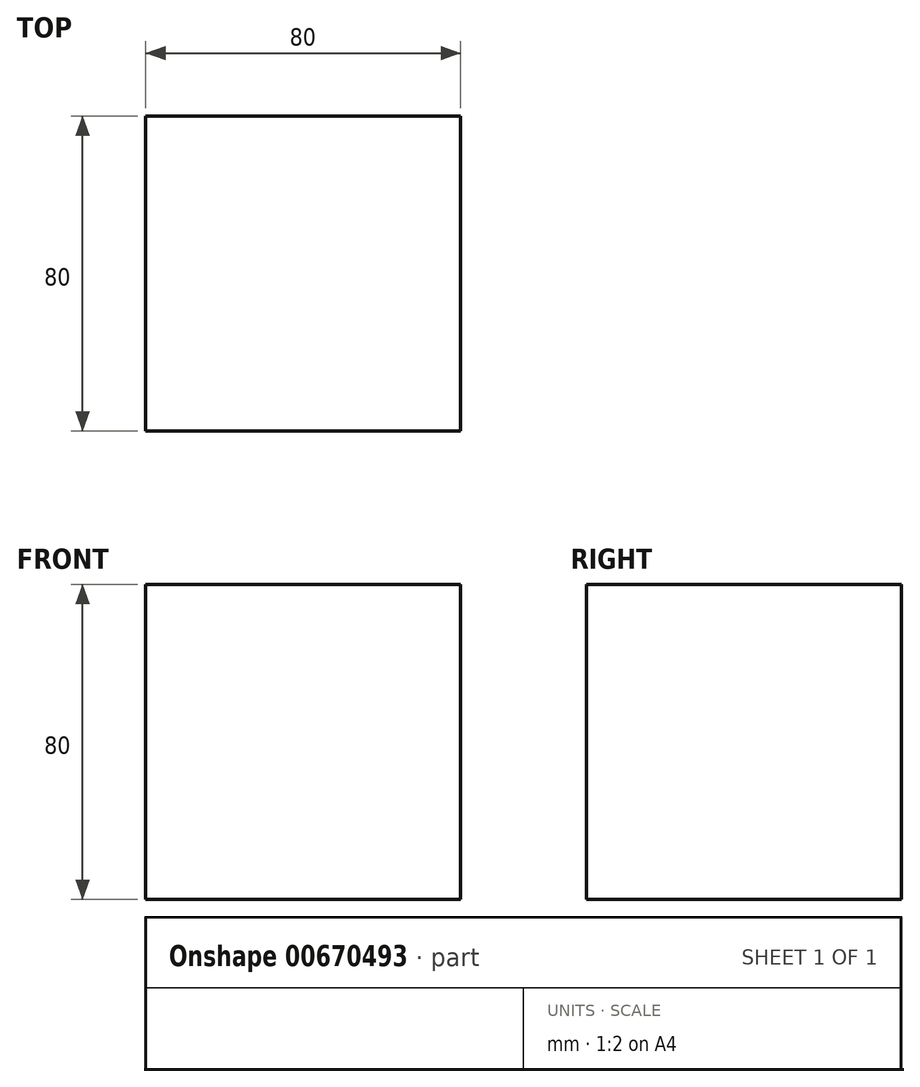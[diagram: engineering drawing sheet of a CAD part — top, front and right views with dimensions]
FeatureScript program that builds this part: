
annotation { "Feature Type Name" : "Feature", "Feature Type Description" : "" }
export const myFeature = defineFeature(function(context is Context, id is Id, definition is map)
    precondition{}
    {
        {
            var Q0;
            Q0=qCreatedBy(makeId("Top.planeOp"),FACE);
            var sketch = newSketch(context, id + "F0", { "sketchPlane" : qUnion([Q0])});
            skLineSegment(sketch, "E0.bottom", {"start": v(47.34, 0) * mm, "end": v(-32.66, 0) * mm});
            skLineSegment(sketch, "E0.top", {"start": v(47.34, -80) * mm, "end": v(-32.66, -80) * mm});
            skLineSegment(sketch, "E0.left", {"start": v(47.34, 0) * mm, "end": v(47.34, -80) * mm});
            skLineSegment(sketch, "E0.right", {"start": v(-32.66, 0) * mm, "end": v(-32.66, -80) * mm});
            skLineSegment(sketch, "E1", {"start": v(47.34, 0) * mm, "end": v(47.34, 0) * mm});
            skCircle(sketch, "E2", {"center": v(-25.02, -1.7) * mm, "radius": 1.5 * mm});
            skCircle(sketch, "E3", {"center": v(18.56, -15.12) * mm, "radius": 1.5 * mm});
            skLineSegment(sketch, "E4.bottom", {"start": v(0, -22.2) * mm, "end": v(-20, -22.2) * mm});
            skLineSegment(sketch, "E4.top", {"start": v(0, -32.2) * mm, "end": v(-20, -32.2) * mm});
            skLineSegment(sketch, "E4.left", {"start": v(0, -22.2) * mm, "end": v(0, -32.2) * mm});
            skLineSegment(sketch, "E4.right", {"start": v(-20, -22.2) * mm, "end": v(-20, -32.2) * mm});
            skLineSegment(sketch, "E5", {"start": v(-10.82, -32.2) * mm, "end": v(-10.82, -52.2) * mm});
            skLineSegment(sketch, "E6", {"start": v(-10.82, -52.2) * mm, "end": v(19.18, -52.2) * mm});
            skLineSegment(sketch, "E7", {"start": v(-10.82, -47.81) * mm, "end": v(19.18, -47.81) * mm});
            skLineSegment(sketch, "E8.bottom", {"start": v(24.63, -35.42) * mm, "end": v(14.63, -35.42) * mm});
            skLineSegment(sketch, "E8.top", {"start": v(24.63, -45.42) * mm, "end": v(14.63, -45.42) * mm});
            skLineSegment(sketch, "E8.left", {"start": v(24.63, -35.42) * mm, "end": v(24.63, -45.42) * mm});
            skLineSegment(sketch, "E8.right", {"start": v(14.63, -35.42) * mm, "end": v(14.63, -45.42) * mm});
            skLineSegment(sketch, "E9", {"start": v(19.18, -47.81) * mm, "end": v(19.18, -45.42) * mm});
            skLineSegment(sketch, "E10", {"start": v(19.18, -52.2) * mm, "end": v(23.46, -52.2) * mm});
            skLineSegment(sketch, "E11", {"start": v(23.46, -52.2) * mm, "end": v(23.46, -45.42) * mm});
            skLineSegment(sketch, "E12.bottom", {"start": v(43.32, -66.85) * mm, "end": v(-26.68, -66.85) * mm});
            skLineSegment(sketch, "E12.top", {"start": v(43.32, -76.7) * mm, "end": v(-28.41, -76.7) * mm});
            skLineSegment(sketch, "E12.left", {"start": v(43.32, -66.85) * mm, "end": v(43.32, -76.7) * mm});
            skLineSegment(sketch, "E12.right", {"start": v(-26.68, -66.85) * mm, "end": v(-28.41, -76.7) * mm});
            skLineSegment(sketch, "E13.bottom", {"start": v(-1.5, -24.06) * mm, "end": v(-18.5, -24.06) * mm});
            skLineSegment(sketch, "E13.top", {"start": v(-1.5, -30.38) * mm, "end": v(-18.5, -30.38) * mm});
            skLineSegment(sketch, "E13.left", {"start": v(-1.5, -24.06) * mm, "end": v(-1.5, -30.38) * mm});
            skLineSegment(sketch, "E13.right", {"start": v(-18.5, -24.06) * mm, "end": v(-18.5, -30.38) * mm});
            skPoint(sketch, "E14", {"position": v(-15.12, -7.6) * mm});
            skPoint(sketch, "E15", {"position": v(-13.48, -3.35) * mm});
            skPoint(sketch, "E16", {"position": v(-5.42, -3.35) * mm});
            skPoint(sketch, "E17", {"position": v(-5.2, -3.35) * mm});
            skPoint(sketch, "E18", {"position": v(-8.25, -3.35) * mm});
            skPoint(sketch, "E19", {"position": v(-9.34, -3.35) * mm});
            skPoint(sketch, "E20", {"position": v(-10.54, -3.35) * mm});
            skPoint(sketch, "E21", {"position": v(-11.52, -3.35) * mm});
            skLineSegment(sketch, "E22", {"start": v(-15.12, -7.6) * mm, "end": v(-15.12, -22.2) * mm});
            skLineSegment(sketch, "E23", {"start": v(-13.48, -3.35) * mm, "end": v(-13.48, -22.2) * mm});
            skLineSegment(sketch, "E24", {"start": v(-10.54, -3.35) * mm, "end": v(-10.54, -22.2) * mm});
            skLineSegment(sketch, "E25", {"start": v(-11.52, -3.35) * mm, "end": v(-11.52, -22.2) * mm});
            skLineSegment(sketch, "E26", {"start": v(-9.34, -3.35) * mm, "end": v(-9.34, -22.2) * mm});
            skLineSegment(sketch, "E27", {"start": v(-8.25, -3.35) * mm, "end": v(-8.25, -22.2) * mm});
            skLineSegment(sketch, "E28", {"start": v(-5.2, -3.35) * mm, "end": v(-5.2, -22.2) * mm});
            skLineSegment(sketch, "E29", {"start": v(-5.42, -3.35) * mm, "end": v(-5.42, -22.2) * mm});
            skLineSegment(sketch, "E30", {"start": v(-20, -27.2) * mm, "end": v(-30.25, -27.2) * mm});
            skLineSegment(sketch, "E31", {"start": v(-30.25, -27.2) * mm, "end": v(-30.25, -76.92) * mm});
            skLineSegment(sketch, "E32", {"start": v(-30.25, -76.92) * mm, "end": v(-26.71, -76.7) * mm});
            skLineSegment(sketch, "E33", {"start": v(-30.25, -73.39) * mm, "end": v(-27.55, -73.86) * mm});
            skPoint(sketch, "E33.endSnap0", {"position": v(-27.55, -71.77) * mm});
            skLineSegment(sketch, "E34.bottom", {"start": v(-22.08, -14.98) * mm, "end": v(-22.08, -14.98) * mm});
            skLineSegment(sketch, "E34.top", {"start": v(-22.08, -14.98) * mm, "end": v(-22.08, -14.98) * mm});
            skLineSegment(sketch, "E34.left", {"start": v(-22.08, -14.98) * mm, "end": v(-22.08, -14.98) * mm});
            skLineSegment(sketch, "E34.right", {"start": v(-22.08, -14.98) * mm, "end": v(-22.08, -14.98) * mm});
            skLineSegment(sketch, "E35", {"start": v(-22.08, -6.35) * mm, "end": v(-22.08, -6.35) * mm});
            skLineSegment(sketch, "E36", {"start": v(32.94, -17.81) * mm, "end": v(19.73, -16.05) * mm});
            skLineSegment(sketch, "E37", {"start": v(-22.08, -1.7) * mm, "end": v(-22.08, -1.7) * mm});
            skLineSegment(sketch, "E38", {"start": v(-22.08, 3.3) * mm, "end": v(-22.08, 3.3) * mm});
            skArc(sketch, "E39", {"start": v(-21.64, -7.78) * mm, "mid": v(-21.25, -7.6) * mm, "end": v(-20.93, -7.3) * mm});
            skArc(sketch, "E40", {"start": v(-20.93, -7.3) * mm, "mid": v(-20.63, -6.75) * mm, "end": v(-20.6, -6.12) * mm});
            skLineSegment(sketch, "E41", {"start": v(-20.6, -6.12) * mm, "end": v(-20.6, -6.12) * mm});
            skArc(sketch, "E42", {"start": v(-20.6, -6.12) * mm, "mid": v(-23.35, -5.55) * mm, "end": v(-21.64, -7.78) * mm});
            skSolve(sketch);
        }
        {
            var Q0;
            Q0=makeQuery(id+"F0.imprint","IMPRINT",FACE,{"disambiguationData":[TD([[makeQuery(id+"F0.imprint","IMPRINT",EDGE,{"derivedFrom":sQuery(id+"F0.wireOp",EDGE,"E0.bottom")}),1.0]])]});
            var Q1;
            Q1=makeQuery(id+"F0.imprint","IMPRINT",FACE,{"disambiguationData":[TD([[makeQuery(id+"F0.imprint","IMPRINT",EDGE,{"derivedFrom":sQuery(id+"F0.wireOp",EDGE,"E2")}),1.0]])]});
            var Q2;
            {var subQ0=sQuery(id+"F0.wireOp",EDGE,"E4.left");Q2=makeQuery(id+"F0.imprint","IMPRINT",FACE,{"disambiguationData":[TD([[makeQuery(id+"F0.imprint","IMPRINT",EDGE,{"derivedFrom":subQ0}),-1.0]])]});}
            var Q3;
            Q3=makeQuery(id+"F0.imprint","IMPRINT",FACE,{"disambiguationData":[TD([[makeQuery(id+"F0.imprint","IMPRINT",EDGE,{"derivedFrom":sQuery(id+"F0.wireOp",EDGE,"E39")}),1.0]])]});
            var Q4;
            Q4=makeQuery(id+"F0.imprint","IMPRINT",FACE,{"disambiguationData":[TD([[makeQuery(id+"F0.imprint","IMPRINT",EDGE,{"derivedFrom":sQuery(id+"F0.wireOp",EDGE,"E13.bottom")}),1.0]])]});
            var Q5;
            Q5=makeQuery(id+"F0.imprint","IMPRINT",FACE,{"disambiguationData":[TD([[makeQuery(id+"F0.imprint","IMPRINT",EDGE,{"derivedFrom":sQuery(id+"F0.wireOp",EDGE,"E3")}),1.0]])]});
            var Q6;
            Q6=makeQuery(id+"F0.imprint","IMPRINT",FACE,{"disambiguationData":[TD([[makeQuery(id+"F0.imprint","IMPRINT",EDGE,{"derivedFrom":sQuery(id+"F0.wireOp",EDGE,"E8.bottom")}),1.0]])]});
            var Q7;
            {var subQ1=sQuery(id+"F0.wireOp",EDGE,"E6");Q7=makeQuery(id+"F0.imprint","IMPRINT",FACE,{"disambiguationData":[TD([[makeQuery(id+"F0.imprint","IMPRINT",EDGE,{"derivedFrom":subQ1}),1.0]])]});}
            var Q8;
            {var subQ5=sQuery(id+"F0.wireOp",EDGE,"E12.bottom");Q8=makeQuery(id+"F0.imprint","IMPRINT",FACE,{"disambiguationData":[TD([[makeQuery(id+"F0.imprint","IMPRINT",EDGE,{"derivedFrom":subQ5}),1.0]])]});}
            var Q9;
            {var subQ0=sQuery(id+"F0.wireOp",EDGE,"E32");Q9=makeQuery(id+"F0.imprint","IMPRINT",FACE,{"disambiguationData":[TD([[makeQuery(id+"F0.imprint","IMPRINT",EDGE,{"derivedFrom":subQ0}),1.0]])]});}
            var Q10;
            Q10=sQuery(id+"F0.wireOp",EDGE,"E0.top");
            var Q11;
            Q11=sQuery(id+"F0.wireOp",EDGE,"E0.left");
            var Q12;
            Q12=sQuery(id+"F0.wireOp",EDGE,"E0.bottom");
            var Q13;
            Q13=sQuery(id+"F0.wireOp",EDGE,"E0.right");
            extrude(context, id + "F1", {"entities" : qUnion([Q0, Q1, Q2, Q3, Q4, Q5, Q6, Q7, Q8, Q9]), "surfaceEntities" : qUnion([Q10, Q11, Q12, Q13]), "depth" : 80 * mm, "offsetDistance" : 25 * mm});
        }
    });
